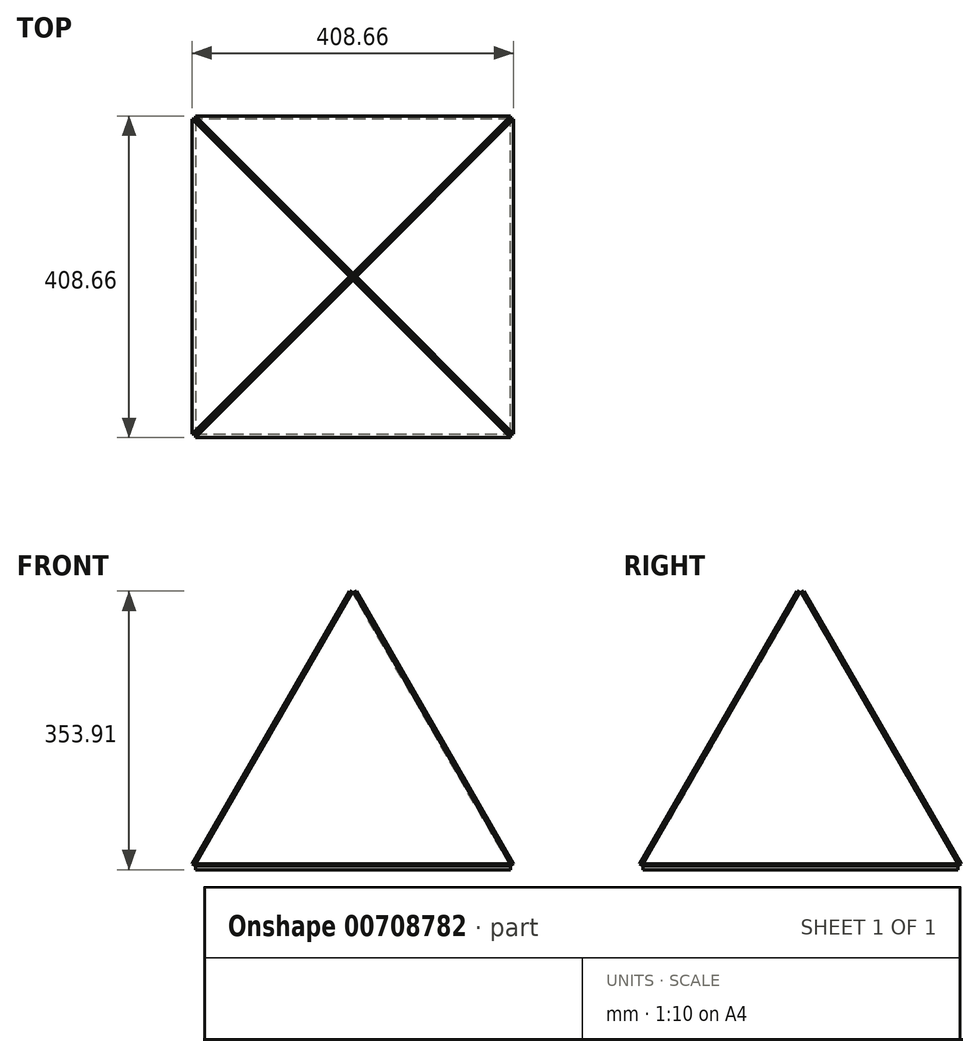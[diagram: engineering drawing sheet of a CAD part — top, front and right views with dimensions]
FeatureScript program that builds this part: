
annotation { "Feature Type Name" : "Feature", "Feature Type Description" : "" }
export const myFeature = defineFeature(function(context is Context, id is Id, definition is map)
    precondition{}
    {
        {
            var Q0;
            Q0=qCreatedBy(makeId("Top.planeOp"),FACE);
            var sketch = newSketch(context, id + "F0", { "sketchPlane" : qUnion([Q0])});
            skLineSegment(sketch, "E0.bottom", {"start": v(-200, -200) * mm, "end": v(200, -200) * mm});
            skLineSegment(sketch, "E0.top", {"start": v(-200, 200) * mm, "end": v(200, 200) * mm});
            skLineSegment(sketch, "E0.left", {"start": v(-200, -200) * mm, "end": v(-200, 200) * mm});
            skLineSegment(sketch, "E0.right", {"start": v(200, -200) * mm, "end": v(200, 200) * mm});
            skPoint(sketch, "E0.middle", {"position": v(0, 0) * mm});
            skSolve(sketch);
        }
        {
            var Q0;
            Q0 = qSketchRegion(id + "F0", true);
            extrude(context, id + "F1", {"entities" : qUnion([Q0]), "depth" : 5 * mm, "offsetDistance" : 25 * mm});
        }
        {
            var Q0;
            Q0=qCreatedBy(makeId("Front.planeOp"),FACE);
            var Q1;
            Q1=makeQuery(id+"F1.opExtrude","CAP_EDGE",EDGE,{"disambiguationData":[OSD([sQuery(id+"F0.wireOp",EDGE,"E0.bottom")])],"isStart":false});
            cPlane(context, id + "F2", {"entities" : qUnion([Q0, Q1]), "cplaneType" : CPlaneType.LINE_ANGLE, "offset" : 25 * mm, "angle" : 30 * degree, "oppositeDirection" : true, "width" : 150 * mm, "height" : 150 * mm});
        }
        {
            var Q0;
            Q0=qCreatedBy(id+"F2.planeOp",FACE);
            var sketch = newSketch(context, id + "F3", { "sketchPlane" : qUnion([Q0])});
            skLineSegment(sketch, "E1.0", {"start": v(200, -95.67) * mm, "end": v(-200, -95.67) * mm});
            skLineSegment(sketch, "E2", {"start": v(200, -95.67) * mm, "end": v(0, 304.33) * mm});
            skLineSegment(sketch, "E3", {"start": v(0, 304.33) * mm, "end": v(-200, -95.67) * mm});
            skLineSegment(sketch, "E4", {"start": v(0, 304.33) * mm, "end": v(0, -95.67) * mm, "construction": true});
            skSolve(sketch);
        }
        {
            var Q0;
            Q0=makeQuery(id+"F3.imprint","IMPRINT",FACE,{"disambiguationData":[TD([[makeQuery(id+"F3.imprint","IMPRINT",EDGE,{"derivedFrom":sQuery(id+"F3.wireOp",EDGE,"E1.0")}),-1.0]])]});
            extrude(context, id + "F4", {"entities" : qUnion([Q0]), "oppositeDirection" : true, "depth" : 5 * mm, "offsetDistance" : 25 * mm});
        }
        {
            var Q0;
            Q0=qCreatedBy(makeId("Front.planeOp"),FACE);
            var sketch = newSketch(context, id + "F5", { "sketchPlane" : qUnion([Q0])});
            skLineSegment(sketch, "E5", {"start": v(0, 0) * mm, "end": v(0, 354.1) * mm});
            skSolve(sketch);
        }
        {
            var Q0;
            Q0=makeQuery(id+"F4.opExtrude","SWEPT_BODY",BODY,{"disambiguationData":[OSD([sQuery(id+"F3.wireOp",EDGE,"E1.0"),sQuery(id+"F3.wireOp",EDGE,"E2"),sQuery(id+"F3.wireOp",EDGE,"E3")])]});
            var Q1;
            Q1=sQuery(id+"F5.wireOp",EDGE,"E5");
            circularPattern(context, id + "F6", {"entities" : qUnion([Q0]), "axis" : qUnion([Q1]), "angle" : 360 * degree, "instanceCount" : 4, "equalSpace" : true});
        }
    });
